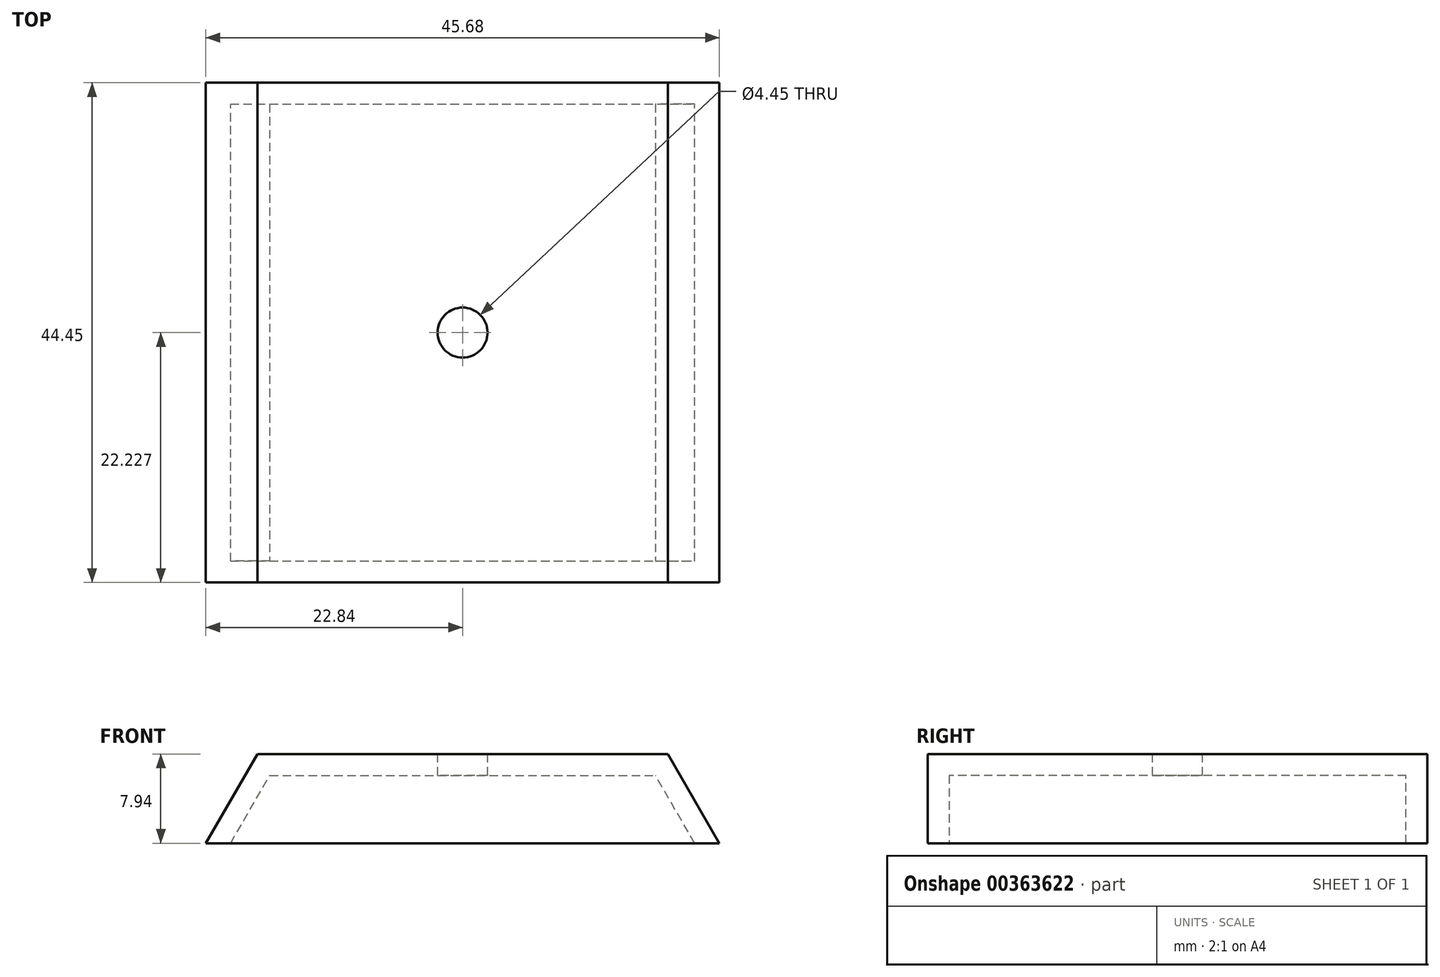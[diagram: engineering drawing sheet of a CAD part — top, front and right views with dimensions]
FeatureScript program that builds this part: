
annotation { "Feature Type Name" : "Feature", "Feature Type Description" : "" }
export const myFeature = defineFeature(function(context is Context, id is Id, definition is map)
    precondition{}
    {
        {
            var Q0;
            Q0=qCreatedBy(makeId("Top.planeOp"),FACE);
            var sketch = newSketch(context, id + "F0", { "sketchPlane" : qUnion([Q0])});
            skLineSegment(sketch, "E0.bottom", {"start": v(-19.2, 39.34) * mm, "end": v(26.83, 39.34) * mm});
            skLineSegment(sketch, "E0.top", {"start": v(-19.2, -5.1) * mm, "end": v(26.83, -5.1) * mm});
            skLineSegment(sketch, "E0.left", {"start": v(-19.2, 39.34) * mm, "end": v(-19.2, -5.1) * mm});
            skLineSegment(sketch, "E0.right", {"start": v(26.83, 39.34) * mm, "end": v(26.83, -5.1) * mm});
            skSolve(sketch);
        }
        {
            var Q0;
            Q0 = qSketchRegion(id + "F0", true);
            extrude(context, id + "F1", {"entities" : qUnion([Q0]), "depth" : 7.94 * mm});
        }
        {
            var Q0;
            Q0=makeQuery(id+"F1.opExtrude","CAP_EDGE",EDGE,{"disambiguationData":[OSD([sQuery(id+"F0.wireOp",EDGE,"E0.left")])],"isStart":false});
            var Q1;
            Q1=makeQuery(id+"F1.opExtrude","CAP_EDGE",EDGE,{"disambiguationData":[OSD([sQuery(id+"F0.wireOp",EDGE,"E0.right")])],"isStart":false});
            chamfer(context, id + "F2", {"entities" : qUnion([Q0, Q1]), "chamferType" : ChamferType.OFFSET_ANGLE, "width" : 4.76 * mm, "oppositeDirection" : false, "angle" : 60 * degree, "tangentPropagation" : true});
        }
        {
            var Q0;
            Q0=makeQuery(id+"F1.opExtrude","CAP_FACE",FACE,{"disambiguationData":[OSD([sQuery(id+"F0.wireOp",EDGE,"E0.bottom"),sQuery(id+"F0.wireOp",EDGE,"E0.top"),sQuery(id+"F0.wireOp",EDGE,"E0.left"),sQuery(id+"F0.wireOp",EDGE,"E0.right")])],"isStart":true});
            shell(context, id + "F3", {"entities" : qUnion([Q0]), "thickness" : 1.9 * mm});
        }
        {
            var Q0;
            Q0=makeQuery(id+"F1.opExtrude","CAP_FACE",FACE,{"disambiguationData":[OSD([sQuery(id+"F0.wireOp",EDGE,"E0.bottom"),sQuery(id+"F0.wireOp",EDGE,"E0.top"),sQuery(id+"F0.wireOp",EDGE,"E0.left"),sQuery(id+"F0.wireOp",EDGE,"E0.right")])],"isStart":false});
            var sketch = newSketch(context, id + "F4", { "sketchPlane" : qUnion([Q0])});
            skCircle(sketch, "E1", {"center": v(3.8, 17.12) * mm, "radius": 3.5 * mm});
            skPoint(sketch, "E1.centerSnap0", {"position": v(-14.45, 17.12) * mm});
            skPoint(sketch, "E1.centerSnap1", {"position": v(3.8, 39.34) * mm});
            skSolve(sketch);
        }
        {
            var Q0;
            Q0=sQuery(id+"F4.wireOp",VERTEX,"E1.center");
            var Q1;
            Q1=makeQuery(id+"F1.opExtrude","SWEPT_BODY",BODY,{"disambiguationData":[OSD([sQuery(id+"F0.wireOp",EDGE,"E0.bottom"),sQuery(id+"F0.wireOp",EDGE,"E0.top"),sQuery(id+"F0.wireOp",EDGE,"E0.left"),sQuery(id+"F0.wireOp",EDGE,"E0.right")])]});
            hole(context, id + "F5", {"style" : HoleStyle.SIMPLE, "endStyle" : HoleEndStyle.THROUGH, "holeDiameter" : 4.44 * mm, "isTappedThrough" : true, "tappedDepth" : 12.7 * mm, "tapClearance" : 3, "locations" : qUnion([Q0]), "scope" : qUnion([Q1])});
        }
    });
